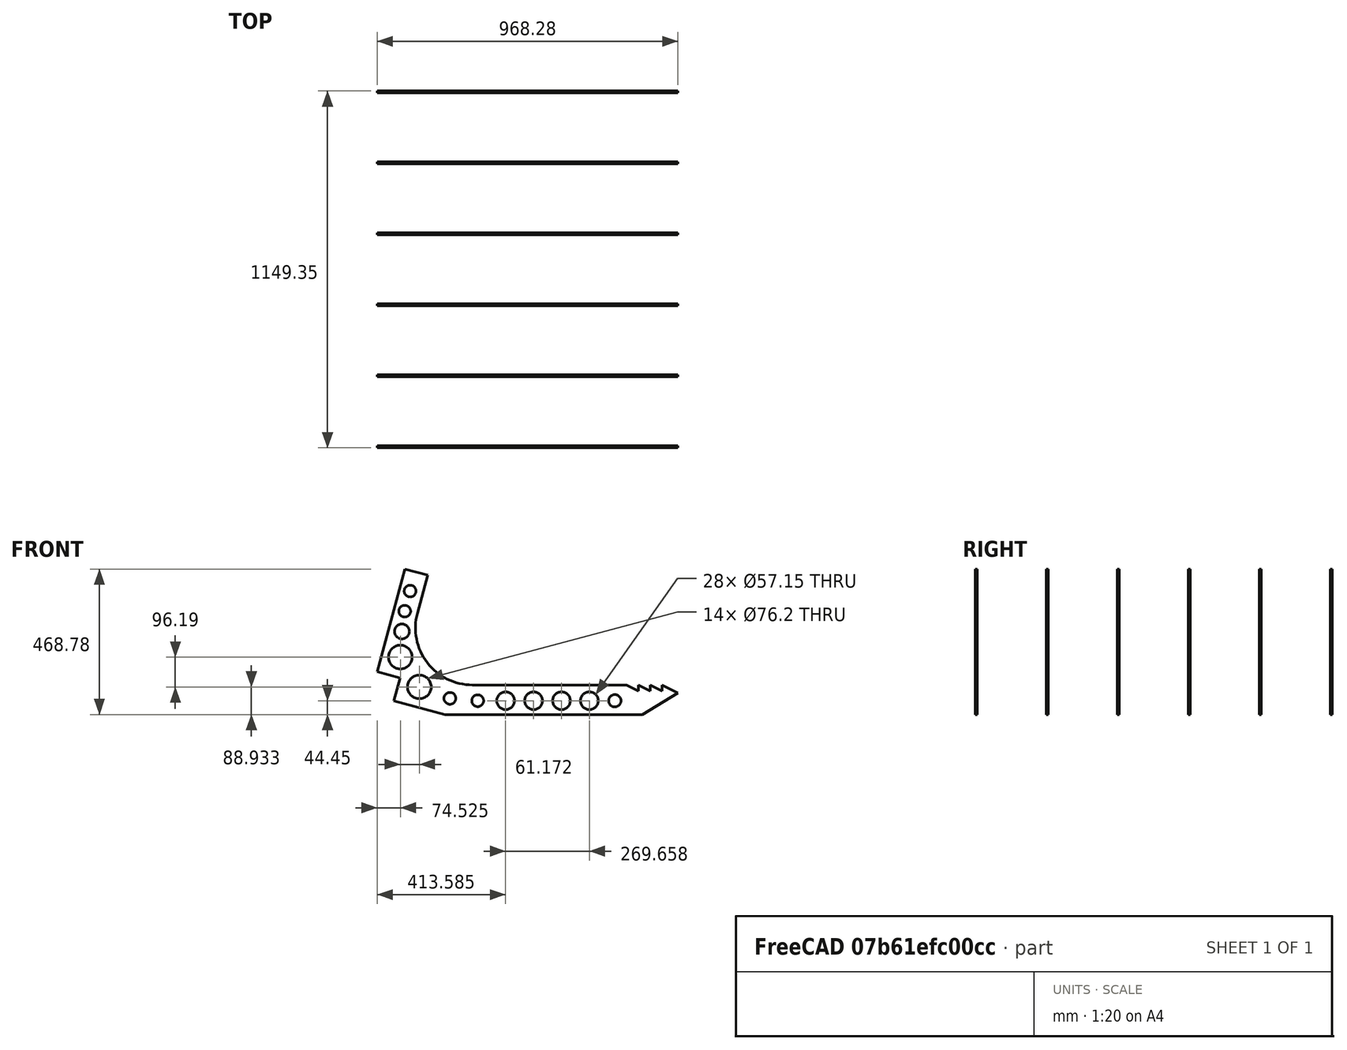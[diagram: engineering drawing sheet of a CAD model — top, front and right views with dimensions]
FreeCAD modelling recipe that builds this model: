
FCSTD DOCUMENT  (FreeCAD 0.17R13522 (Git))
Label: Inside tine
License: CreativeCommons Attribution
LicenseURL: http://creativecommons.org/licenses/by/4.0/
objects: Sketcher::SketchObject×2, Part::FeaturePython×2, PartDesign::Pad×1, PartDesign::Body×1, Fem::FemSolverObjectPython×1, App::MaterialObjectPython×1, Fem::ConstraintForce×1, Fem::ConstraintFixed×1, Fem::FemMeshObjectPython×1, Fem::FemAnalysis×1
note: 7 computed .brp shape members not serialized (recipe doc carries the construction recipe); baked Part::Feature solids carry a one-line shape summary decoded from their .brp

FEATURE [Sketcher::SketchObject] Sketch  label="Inside Tine"
  MapMode = 5
  Placement = pos=(0,0,0) rot=(1,0,0;1.5708rad)
  sketch-geometry (41):
    g0: LineSegment StartX=165.1 StartY=0 StartZ=0 EndX=800.1 EndY=0 EndZ=0
    g1: LineSegment StartX=800.1 StartY=0 StartZ=0 EndX=914.4 EndY=69.85 EndZ=0
    g2: LineSegment StartX=749.3 StartY=95.25 StartZ=0 EndX=252.957 EndY=95.25 EndZ=0
    g3: LineSegment StartX=75.601 StartY=326.385 StartZ=0 EndX=108.471 EndY=449.058 EndZ=0
    g4: LineSegment StartX=108.471 StartY=449.058 StartZ=0 EndX=34.8675 EndY=468.78 EndZ=0
    g5: LineSegment StartX=34.8675 StartY=468.78 StartZ=0 EndX=-53.8815 EndY=137.564 EndZ=0
    g6: LineSegment StartX=165.1 StartY=0 StartZ=0 EndX=0 EndY=44.2384 EndZ=0
    g7: Circle CenterX=711.2 CenterY=44.45 CenterZ=0 NormalX=0 NormalY=0 NormalZ=1 AngleXU=0 Radius=19.8755
    g8: LineSegment StartX=19.722 StartY=117.842 StartZ=0 EndX=0 EndY=44.2384 EndZ=0
    g9: LineSegment [constr] StartX=-73.6035 StartY=63.9604 StartZ=0 EndX=-53.8815 EndY=137.564 EndZ=0
    g10: LineSegment [constr] StartX=-73.6035 StartY=63.9604 StartZ=0 EndX=0 EndY=44.2384 EndZ=0
    g11: LineSegment StartX=19.722 StartY=117.842 StartZ=0 EndX=-53.8815 EndY=137.564 EndZ=0
    g12: LineSegment StartX=914.4 StartY=69.85 StartZ=0 EndX=863.6 EndY=95.25 EndZ=0
    g13: LineSegment StartX=863.6 StartY=95.25 StartZ=0 EndX=863.6 EndY=76.2 EndZ=0
    g14: LineSegment StartX=863.6 StartY=76.2 StartZ=0 EndX=825.5 EndY=95.25 EndZ=0
    g15: LineSegment StartX=825.5 StartY=95.25 StartZ=0 EndX=825.5 EndY=76.2 EndZ=0
    g16: LineSegment StartX=825.5 StartY=76.2 StartZ=0 EndX=787.4 EndY=95.25 EndZ=0
    g17: LineSegment StartX=787.4 StartY=95.25 StartZ=0 EndX=787.4 EndY=76.2 EndZ=0
    g18: LineSegment StartX=787.4 StartY=76.2 StartZ=0 EndX=749.3 EndY=95.25 EndZ=0
    g19: LineSegment [constr] StartX=629.363 StartY=44.45 StartZ=0 EndX=539.477 EndY=44.45 EndZ=0
    g20: LineSegment [constr] StartX=539.477 StartY=44.45 StartZ=0 EndX=449.591 EndY=44.45 EndZ=0
    g21: LineSegment [constr] StartX=449.591 StartY=44.45 StartZ=0 EndX=359.705 EndY=44.45 EndZ=0
    g22: LineSegment [constr] StartX=359.705 StartY=44.45 StartZ=0 EndX=269.819 EndY=44.45 EndZ=0
    g23: LineSegment [constr] StartX=269.819 StartY=44.45 StartZ=0 EndX=180.259 EndY=52.0947 EndZ=0
    g24: LineSegment [constr] StartX=180.259 StartY=52.0947 StartZ=0 EndX=81.8176 EndY=88.9328 EndZ=0
    g25: LineSegment [constr] StartX=69.5262 StartY=462.368 StartZ=0 EndX=52.1707 EndY=397.596 EndZ=0
    g26: LineSegment [constr] StartX=52.1707 StartY=397.596 StartZ=0 EndX=34.8152 EndY=332.825 EndZ=0
    g27: LineSegment [constr] StartX=34.8152 StartY=332.825 StartZ=0 EndX=25.9917 EndY=267.609 EndZ=0
    g28: LineSegment [constr] StartX=25.9917 StartY=267.609 StartZ=0 EndX=20.6454 EndY=185.123 EndZ=0
    g29: Circle CenterX=52.1707 CenterY=397.596 CenterZ=0 NormalX=0 NormalY=0 NormalZ=1 AngleXU=0 Radius=19.05
    g30: Circle CenterX=34.8152 CenterY=332.825 CenterZ=0 NormalX=0 NormalY=0 NormalZ=1 AngleXU=0 Radius=19.05
    g31: Circle CenterX=25.9917 CenterY=267.609 CenterZ=0 NormalX=0 NormalY=0 NormalZ=1 AngleXU=0 Radius=23.8958
    g32: Circle CenterX=20.6454 CenterY=185.123 CenterZ=0 NormalX=0 NormalY=0 NormalZ=1 AngleXU=0 Radius=38.1
    g33: Circle CenterX=629.363 CenterY=44.45 CenterZ=0 NormalX=0 NormalY=0 NormalZ=1 AngleXU=0 Radius=28.575
    g34: Circle CenterX=539.477 CenterY=44.45 CenterZ=0 NormalX=0 NormalY=0 NormalZ=1 AngleXU=0 Radius=28.575
    g35: Circle CenterX=449.591 CenterY=44.45 CenterZ=0 NormalX=0 NormalY=0 NormalZ=1 AngleXU=0 Radius=28.575
    g36: Circle CenterX=359.705 CenterY=44.45 CenterZ=0 NormalX=0 NormalY=0 NormalZ=1 AngleXU=0 Radius=28.575
    g37: Circle CenterX=269.819 CenterY=44.45 CenterZ=0 NormalX=0 NormalY=0 NormalZ=1 AngleXU=0 Radius=19.05
    g38: Circle CenterX=180.259 CenterY=52.0947 CenterZ=0 NormalX=0 NormalY=0 NormalZ=1 AngleXU=0 Radius=19.05
    g39: Circle CenterX=81.8176 CenterY=88.9328 CenterZ=0 NormalX=0 NormalY=0 NormalZ=1 AngleXU=0 Radius=38.1
    g40: ArcOfCircle CenterX=252.957 CenterY=278.863 CenterZ=0 NormalX=0 NormalY=0 NormalZ=1 AngleXU=0 Radius=183.613 StartAngle=2.87979 EndAngle=4.71239
  constraints (99):
    c: Horizontal(g0)
    c: Coincident(g0,g1)
    c: Horizontal(g2)
    c: Coincident(g3,g4)
    c: Coincident(g4,g5)
    c: Parallel(g3,g5)
    c: Perpendicular(g4,g3)
    c: Coincident(g0,g6)
    c: PointOnObject(g0,g-1)
    c: Angle(g-2,g5) = 2.87979
    c: Distance(g3) = 127
    c: Perpendicular(g5,g6)
    c: Radius(g7) = 19.8755
    c: Perpendicular(g6,g8)
    c: Coincident(g6,g8)
    c: Coincident(g9,g5)
    c: Coincident(g10,g6)
    c: Distance(g8) = 76.2
    c: Parallel(g10,g6)
    c: Parallel(g9,g5)
    c: Distance(g4,g9) = 419.1
    c: Coincident(g10,g9)
    c: PointOnObject(g6,g-2)
    c: PointOnObject(g8,g3)
    c: Coincident(g11,g8)
    c: Coincident(g11,g5)
    c: Perpendicular(g8,g11)
    c: DistanceX(g-1,g0) = 165.1
    c: Distance(g4) = 76.2
    c: Vertical(g13)
    c: Coincident(g13,g14)
    c: PointOnObject(g15,g2)
    c: Vertical(g15)
    c: Coincident(g15,g16)
    c: PointOnObject(g17,g2)
    c: Vertical(g17)
    c: Coincident(g17,g18)
    c: Parallel(g18,g16)
    c: Parallel(g16,g14)
    c: Parallel(g14,g12)
    c: Equal(g13,g15)
    c: Equal(g15,g17)
    c: Equal(g14,g16)
    c: Equal(g16,g18)
    c: DistanceY(g13,g13) = 19.05
    c: DistanceX(g15,g14) = 38.1
    c: DistanceX(g-1,g0) = 800.1
    c: Coincident(g2,g18)
    c: Coincident(g12,g13)
    c: Coincident(g15,g14)
    c: Coincident(g16,g17)
    c: Coincident(g1,g12)
    c: DistanceY(g0,g12) = 95.25
    c: DistanceX(g12,g1) = 50.8
    c: DistanceX(g-1,g7) = 711.2
    c: DistanceX(g-1,g1) = 914.4
    c: Horizontal(g19)
    c: Coincident(g19,g20)
    c: Horizontal(g20)
    c: Coincident(g20,g21)
    c: Horizontal(g21)
    c: Coincident(g21,g22)
    c: Horizontal(g22)
    c: Coincident(g22,g23)
    c: Coincident(g23,g24)
    c: Coincident(g25,g26)
    c: Coincident(g26,g27)
    c: Coincident(g27,g28)
    c: Equal(g19,g20)
    c: Equal(g20,g21)
    c: Equal(g21,g22)
    c: Equal(g22,g23)
    c: Equal(g25,g26)
    c: Parallel(g25,g26)
    c: Coincident(g29,g25)
    c: Coincident(g30,g26)
    c: Coincident(g31,g27)
    c: Coincident(g32,g28)
    c: Coincident(g33,g19)
    c: Coincident(g34,g19)
    c: Coincident(g35,g20)
    c: Coincident(g36,g21)
    c: Coincident(g37,g22)
    c: Coincident(g38,g23)
    c: Coincident(g39,g24)
    c: Radius(g33) = 28.575
    c: Equal(g33,g34)
    c: Equal(g33,g35)
    c: Equal(g33,g36)
    c: Distance(g19,g0) = 44.45
    c: Radius(g32) = 38.1
    c: Parallel(g25,g5)
    c: Equal(g37,g38)
    c: Radius(g39) = 38.1
    c: Tangent(g2,g40) = 1.5708
    c: Coincident(g40,g3)
    c: Tangent(g40,g3)
    c: PointOnObject(g7,g19)
    c: Radius(g38) = 19.05
FEATURE [PartDesign::Pad] Pad
  Length = 6.35
  Length2 = 100.076
  Placement = pos=(0,0,0) rot=(1,0,0;1.5708rad)
  Profile = -> Sketch
  Type = 0
FEATURE [PartDesign::Body] Body
  Group = -> [Sketch,Pad]
  Origin = -> Origin
  Tip = -> Pad
FEATURE [Part::FeaturePython] Array  # Draft array (typed FeaturePython)
  Angle = 360
  ArrayType = 0
  Axis = (0,0,1)
  Base = -> Body
  Center = (0,0,0)
  Fuse = false
  IntervalAxis = (0,0,0)
  IntervalX = (1,0,0)
  IntervalY = (0,228.6,0)
  IntervalZ = (0,0,0)
  NumberPolar = 1
  NumberX = 1
  NumberY = 6
  NumberZ = 1
FEATURE [Part::FeaturePython] Clone  label="Body001"  # Draft clone (typed FeaturePython)
  AttacherType = Attacher::AttachEngine3D
  Fuse = false
  Objects = -> [Body]
  Scale = (1,1,1)
FEATURE [Fem::FemSolverObjectPython] CalculiXccxTools  # FEM object (typed FeaturePython)
  AnalysisType = 0
  BeamShellResultOutput3D = false
  EigenmodeHighLimit = 1000000
  EigenmodeLowLimit = 0
  EigenmodesCount = 10
  GeometricalNonlinearity = 0
  IterationsControlParameterCutb = 0.25,0.5,0.75,0.85,,,1.5,
  IterationsControlParameterIter = 4,8,9,200,10,400,,200,,
  IterationsControlParameterTimeUse = false
  IterationsThermoMechMaximum = 2000
  IterationsUserDefinedIncrementations = false
  IterationsUserDefinedTimeStepLength = false
  MaterialNonlinearity = 0
  MatrixSolverType = 0
  SplitInputWriter = false
  ThermoMechSteadyState = true
  TimeEnd = 1
  TimeInitialStep = 0.01
FEATURE [App::MaterialObjectPython] SolidMaterial  # material (typed FeaturePython)
  Category = 0
  Material = Density=7900 kg/m^3,Description=Standard steel material for CalculiX sample calculations,Father=Metal,Name=CalculiX-Steel,PoissonRatio=0.7,+4 more (map truncated)
FEATURE [Sketcher::SketchObject] Sketch001
  Placement = pos=(0,0,0) rot=(1,0,0;1.5708rad)
  sketch-geometry (7):
    g0: LineSegment StartX=596.9 StartY=292.1 StartZ=0 EndX=588.753 EndY=458.61 EndZ=0
    g1: LineSegment StartX=588.753 StartY=458.61 StartZ=0 EndX=440.478 EndY=534.81 EndZ=0
    g2: LineSegment StartX=440.478 StartY=534.81 StartZ=0 EndX=300.349 EndY=444.5 EndZ=0
    g3: LineSegment StartX=300.349 StartY=444.5 StartZ=0 EndX=308.495 EndY=277.99 EndZ=0
    g4: LineSegment StartX=308.495 StartY=277.99 StartZ=0 EndX=456.771 EndY=201.79 EndZ=0
    g5: LineSegment StartX=456.771 StartY=201.79 StartZ=0 EndX=596.9 EndY=292.1 EndZ=0
    g6: Circle [constr] CenterX=448.624 CenterY=368.3 CenterZ=0 NormalX=0 NormalY=0 NormalZ=1 AngleXU=0 Radius=166.71
  constraints (13):
    c: Coincident(g0,g1)
    c: Coincident(g1,g2)
    c: Coincident(g2,g3)
    c: Coincident(g3,g4)
    c: Coincident(g4,g5)
    c: Coincident(g5,g0)
    c: Equal(g0, g1-g5) x5
    c: PointOnObject(g0,g6)
    c: PointOnObject(g1,g6)
    c: PointOnObject(g2,g6)
    c: PointOnObject(g3,g6)
    c: PointOnObject(g4,g6)
    c: PointOnObject(g5,g6)
FEATURE [Fem::ConstraintForce] FemConstraintForce
  Direction = -> Sketch001 [Edge4]
  DirectionVector = (0.0488675,0,-0.998805)
  Force = 16000
  NormalDirection = (0.447214,0,0.894427)
  Points = (12) [(914.4,-6.35,69.85),(897.467,-6.35,78.3167),(880.533,-6.35,86.7833),(863.6,-6.35,95.25),(914.4,-3.175,69.85),(897.467,-3.175,78.3167),+6 more]
  References = -> [Clone]
  Scale = 4
FEATURE [Fem::ConstraintFixed] FemConstraintFixed
  NormalDirection = (0.258819,0,0.965926)
  Normals = (12) [(0.258819,3.21718e-16,0.965926),(0.258819,3.21718e-16,0.965926),(0.258819,3.21718e-16,0.965926),(0.258819,3.21718e-16,0.965926),+8 more]
  Points = (12) [(108.471,-6.35,449.058),(83.9365,-6.35,455.632),(59.402,-6.35,462.206),(34.8675,-6.35,468.78),(108.471,-3.175,449.058),(83.9365,-3.175,455.632),+6 more]
  References = -> [Clone]
  Scale = 5
FEATURE [Fem::FemMeshObjectPython] FEMMeshGmsh  # FEM object (typed FeaturePython)
  Algorithm2D = 0
  Algorithm3D = 0
  CharacteristicLengthMax = 2.54
  CharacteristicLengthMin = 0
  CoherenceMesh = true
  ElementDimension = 2
  ElementOrder = 1
  GeometryTolerance = 1e-06
  GroupsOfNodes = false
  HighOrderOptimize = false
  OptimizeNetgen = false
  OptimizeStd = true
  Part = -> Clone
  RecombineAll = false
FEATURE [Fem::FemAnalysis] Analysis
  Group = -> [CalculiXccxTools,SolidMaterial,FemConstraintForce,FemConstraintFixed,FEMMeshGmsh]
